# Revit family: Kombiventil 4001
name_source: partatom
category: Rohrzubehör
units: mm (PartAtom-declared; Revit-internal decimal feet)

## family parameters
Arbeitsebenenbasiert = Nein
Beim Laden mit Abzugskörper schneiden = Nein
Bemaßung runder Anschluss = Durchmesser verwenden
Gemeinsam genutzt = Nein
Immer vertikal = Ja
OmniClass-Nummer = 23.65.55.14
OmniClass-Titel = Valves for Liquid Services
Teiletyp = Unterbricht

## types (1)
- Kombiventil 4001
    Anwendungsgebiet = Der Volumenstromregler wird in Heiz- und Kühlanlagen mit Umwälzpumpen eingesetzt. Der Regler begrenzt automatisch
den Volumenstrom im nachstehendem Bereich auf den einmal eingestellten Wert indem alle Druckschwankungen
gemessen und ausgeregelt werden. Somit sind keine Messungen erforderlich, und die Regelung ist bei
allen Betriebsbedingungen effektiv. Der Volumenstromregler regelt den Volumenstrom gemäß der Voreinstellung
auf einen konstanten Wert; die Membrane regelt aufgrund des Druckes unmittelbar nach dem Regeleinsatz (über
eine interne Steuerleitung), sowie des Druckes davor. Die Voreinstellung bezieht sich direkt auf den Volumenstrom;
entsprechend kann die Maximal-Durchflußmenge bei der Montage direkt nach Diagramm eingestellt werden. Somit
sind z.B. Heizungsstränge, Kühlwasserkreisläufe, Deckenstrahlplatten, Kühldecken und Lufterhitzer ohne Rücksicht
auf die Druckverteilung in der Anlage ohne weiteres abgleichbar.
    Gehäuse = entzinkunsbeständiges Messing
    H05 = 9 mm  [stored 0.0295276 ft]
    H07 = 4 mm  [stored 0.0131234 ft]
    H09 = 21.8 mm  [stored 0.0715223 ft]
    H12 = 19.25 mm  [stored 0.0631562 ft]
    Hersteller = HERZ Armaturen Ges.m.b.H.
    L02 = 43.5 mm  [stored 0.142717 ft]
    L03 = 3.2 mm  [stored 0.0104987 ft]
    L04 = 1.5 mm  [stored 0.00492126 ft]
    L05 = 11 mm  [stored 0.0360892 ft]
    Max. Betriebsdruck = 1600000.0 Pa
    Max. Betriebstemperatur ab DN40 = 110 °C
    Max. Betriebstemperatur bis DN32 = 130 °C
    Medium = Wasserbeschaffenheit nach ÖNORM H 5195 und VDI 2035
Die Verwendung von Ethylen- und Propylenglykol ist im Mischungsverhältnis 25 - 50 Vol. [%] zulässig
    Membrane und O-Ringe = EPDM
    Min. Betriebstemperatur (Frostschutz) = -20 °C
    Min. Betriebstemperatur (reines Wasser) = 2 °C
    PN = 16
    R04 = 12.5 mm  [stored 0.0410105 ft]
    R05 = 15 mm  [stored 0.0492126 ft]
    R08 = 11.3 mm  [stored 0.0370735 ft]
    R09 = 18.25 mm  [stored 0.0598753 ft]
    R10 = 35 mm  [stored 0.114829 ft]
    R11 = 6.5 mm
    R12 = 3.9 mm  [stored 0.0127953 ft]
    S01 = 10 mm  [stored 0.0328084 ft]
    SCRNCODE = 05;04;02
    SCRNSEQ = ARM;ARM_TYP="DURR";2
    URL = www.herz-armaturen.at
    VRL02 = 18 mm  [stored 0.0590551 ft]
    VRL04 = 8 mm  [stored 0.0262467 ft]
    Vorgabe-Ansicht = 0 mm  [stored 0 ft]

note: [stored X ft] marks values corroborated as IEEE doubles in the binary element streams (Revit-internal decimal feet)
